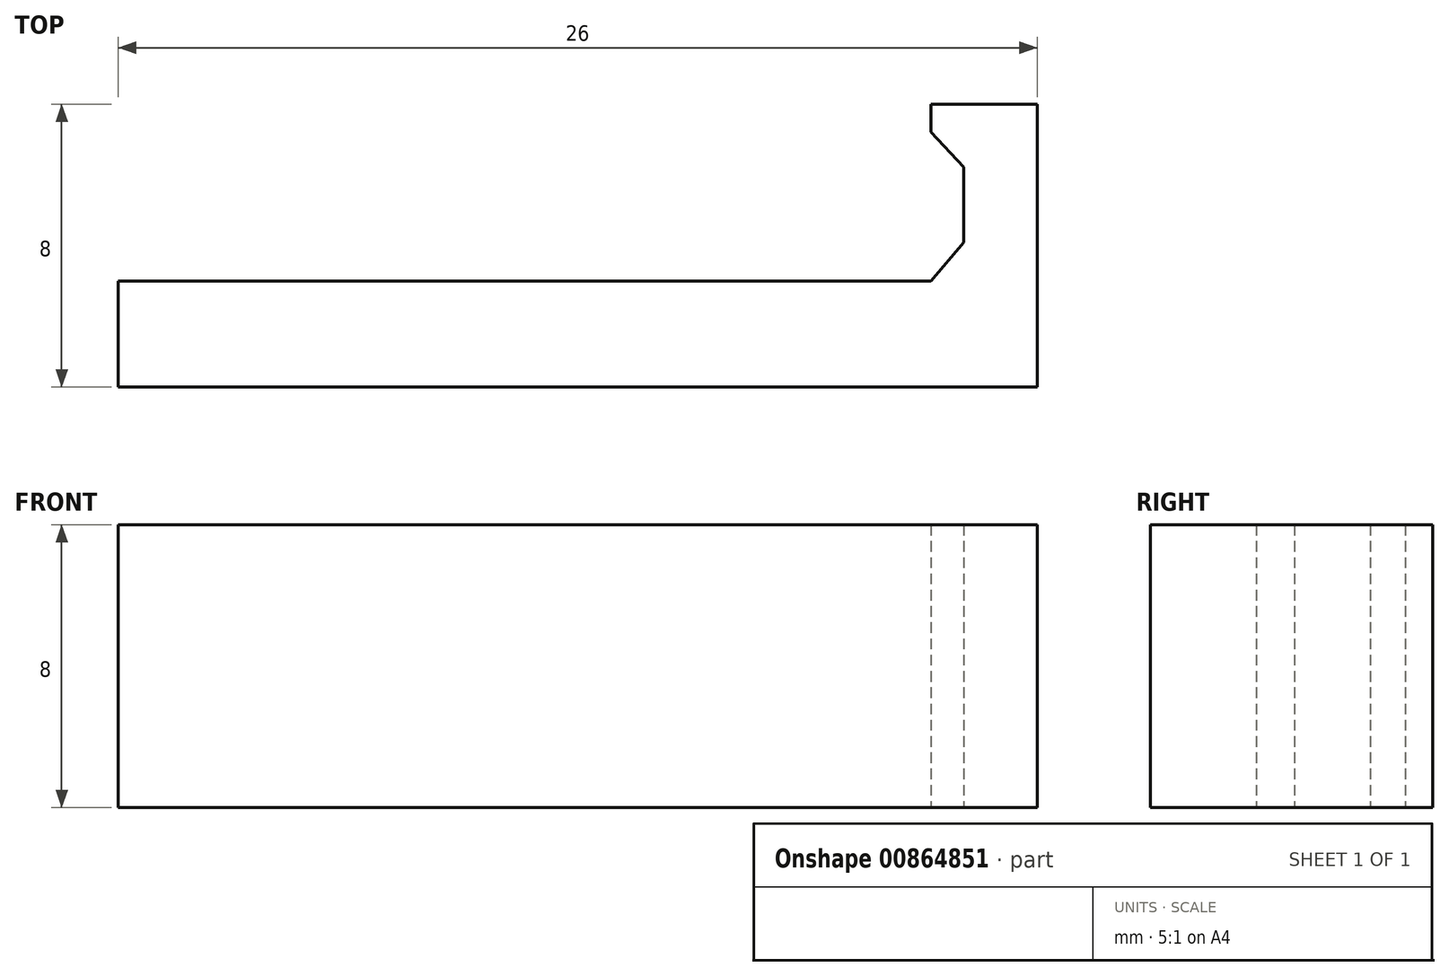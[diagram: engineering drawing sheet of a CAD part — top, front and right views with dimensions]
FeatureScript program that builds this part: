
annotation { "Feature Type Name" : "Feature", "Feature Type Description" : "" }
export const myFeature = defineFeature(function(context is Context, id is Id, definition is map)
    precondition{}
    {
        {
            var Q0;
            Q0=qCreatedBy(makeId("Top.planeOp"),FACE);
            var sketch = newSketch(context, id + "F0", { "sketchPlane" : qUnion([Q0])});
            skLineSegment(sketch, "E0", {"start": v(0, 0) * mm, "end": v(25, 0) * mm});
            skLineSegment(sketch, "E1", {"start": v(25, 0) * mm, "end": v(25, 8) * mm});
            skLineSegment(sketch, "E2", {"start": v(25, 8) * mm, "end": v(23, 8) * mm});
            skLineSegment(sketch, "E3", {"start": v(23, 8) * mm, "end": v(18, 3) * mm});
            skLineSegment(sketch, "E4", {"start": v(18, 3) * mm, "end": v(0, 3) * mm});
            skLineSegment(sketch, "E5", {"start": v(0, 3) * mm, "end": v(0, 0) * mm});
            skSolve(sketch);
        }
        {
            var Q0;
            Q0=qCreatedBy(makeId("Top.planeOp"),FACE);
            var sketch = newSketch(context, id + "F1", { "sketchPlane" : qUnion([Q0])});
            skLineSegment(sketch, "E6", {"start": v(0, 0) * mm, "end": v(26, 0) * mm});
            skLineSegment(sketch, "E7", {"start": v(26, 0) * mm, "end": v(26, 8) * mm});
            skLineSegment(sketch, "E8", {"start": v(26, 8) * mm, "end": v(23, 8) * mm});
            skLineSegment(sketch, "E9", {"start": v(18, 3) * mm, "end": v(0, 3) * mm});
            skLineSegment(sketch, "E10", {"start": v(0, 3) * mm, "end": v(0, 0) * mm});
            skLineSegment(sketch, "E11", {"start": v(23, 8) * mm, "end": v(23, 7.21) * mm});
            skLineSegment(sketch, "E12", {"start": v(23, 7.21) * mm, "end": v(23.92, 6.22) * mm});
            skLineSegment(sketch, "E13", {"start": v(23.92, 6.22) * mm, "end": v(23.92, 4.08) * mm});
            skLineSegment(sketch, "E14", {"start": v(23.92, 4.08) * mm, "end": v(23, 3) * mm});
            skLineSegment(sketch, "E15", {"start": v(23, 3) * mm, "end": v(18, 3) * mm});
            skSolve(sketch);
        }
        {
            var Q0;
            Q0=makeQuery(id+"F1.imprint","IMPRINT",FACE,{"disambiguationData":[TD([[makeQuery(id+"F1.imprint","IMPRINT",EDGE,{"derivedFrom":sQuery(id+"F1.wireOp",EDGE,"E6")}),1.0]])]});
            extrude(context, id + "F2", {"entities" : qUnion([Q0]), "depth" : 8 * mm, "offsetDistance" : 25 * mm});
        }
    });
